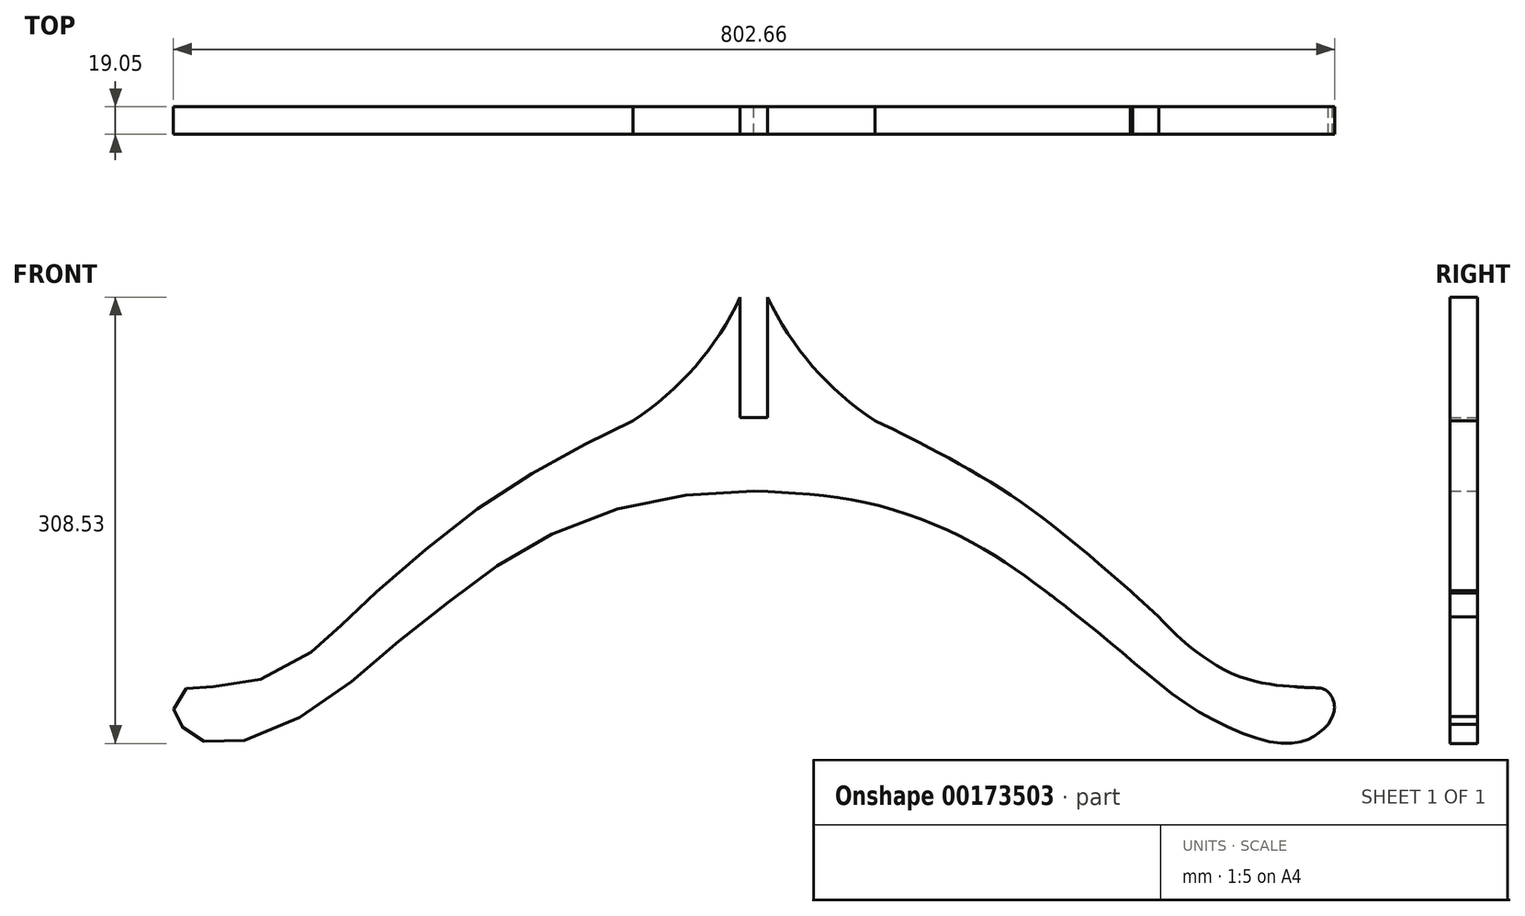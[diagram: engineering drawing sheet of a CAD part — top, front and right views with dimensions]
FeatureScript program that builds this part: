
annotation { "Feature Type Name" : "Feature", "Feature Type Description" : "" }
export const myFeature = defineFeature(function(context is Context, id is Id, definition is map)
    precondition{}
    {
        {
            var Q0;
            Q0=qCreatedBy(makeId("Front.planeOp"),FACE);
            var sketch = newSketch(context, id + "F0", { "sketchPlane" : qUnion([Q0])});
            skLineSegment(sketch, "E0", {"start": v(201.18, -300.83) * mm, "end": v(226.52, -320.33) * mm});
            skLineSegment(sketch, "E1", {"start": v(397.01, -393.15) * mm, "end": v(399.84, -387.85) * mm});
            skLineSegment(sketch, "E2", {"start": v(386.12, -367.88) * mm, "end": v(373.68, -367.2) * mm});
            skLineSegment(sketch, "E3", {"start": v(279.8, -319.03) * mm, "end": v(261.27, -301.84) * mm});
            skLineSegment(sketch, "E4", {"start": v(261.27, -301.84) * mm, "end": v(238.4, -281.97) * mm});
            skArc(sketch, "E5", {"start": v(-83.69, -183.2) * mm, "mid": v(-40.6, -145.75) * mm, "end": v(-9.53, -97.87) * mm});
            skArc(sketch, "E6.MirrorCS", {"start": v(83.69, -183.2) * mm, "mid": v(40.6, -145.75) * mm, "end": v(9.53, -97.87) * mm});
            skLineSegment(sketch, "E7", {"start": v(0, -232) * mm, "end": v(0, -181.2) * mm, "construction": true});
            skLineSegment(sketch, "E8.0", {"start": v(9.53, -97.87) * mm, "end": v(9.53, -181.2) * mm});
            skLineSegment(sketch, "E9.0", {"start": v(-9.53, -97.87) * mm, "end": v(-9.53, -181.2) * mm});
            skLineSegment(sketch, "E10", {"start": v(-9.53, -181.2) * mm, "end": v(9.53, -181.2) * mm});
            skFitSpline(sketch, "E11", {"points": [v(83.69, -183.2) * mm, v(126.62, -204.79) * mm, v(182.9, -238.39) * mm, v(238.4, -281.97) * mm, v(279.8, -319.03) * mm, v(294.96, -334.12) * mm, v(334.74, -359.77) * mm, v(373.68, -367.2) * mm, v(386.12, -367.88) * mm, v(396.38, -370.2) * mm, v(401.31, -380.76) * mm, v(399.84, -387.85) * mm, v(397.01, -393.15) * mm, v(390.26, -399.24) * mm, v(380.3, -404.79) * mm, v(354.8, -404.8) * mm, v(300.62, -380.07) * mm, v(251.38, -340.85) * mm, v(201.18, -300.83) * mm, v(150.22, -267.14) * mm, v(76.14, -239.52) * mm, v(0, -232) * mm], "startDerivative": vector(745.66, -363.57) * mm, "endDerivative": vector(-1080.07, 42.3) * mm});
            skFitSpline(sketch, "E12.MirrorCS", {"points": [v(-83.69, -183.2) * mm, v(-126.62, -204.79) * mm, v(-182.9, -238.39) * mm, v(-238.4, -281.97) * mm, v(-279.8, -319.03) * mm, v(-294.96, -334.12) * mm, v(-334.74, -359.77) * mm, v(-373.68, -367.2) * mm, v(-386.12, -367.88) * mm, v(-396.38, -370.2) * mm, v(-401.31, -380.76) * mm, v(-399.84, -387.85) * mm, v(-397.01, -393.15) * mm, v(-390.26, -399.24) * mm, v(-380.3, -404.79) * mm, v(-354.8, -404.8) * mm, v(-300.62, -380.07) * mm, v(-251.38, -340.85) * mm, v(-201.18, -300.83) * mm, v(-150.22, -267.14) * mm, v(-76.14, -239.52) * mm, v(0, -232) * mm], "startDerivative": vector(-745.66, -363.57) * mm, "endDerivative": vector(1080.07, 42.3) * mm});
            skSolve(sketch);
        }
        {
            var Q0;
            {var subQ17=sQuery(id+"F0.wireOp",EDGE,"E1");Q0=makeQuery(id+"F0.imprint","IMPRINT",FACE,{"disambiguationData":[TD([[makeQuery(id+"F0.imprint","IMPRINT",EDGE,{"derivedFrom":subQ17}),1.0]])]});}
            extrude(context, id + "F1", {"entities" : qUnion([Q0]), "depth" : 19.05 * mm});
        }
    });
